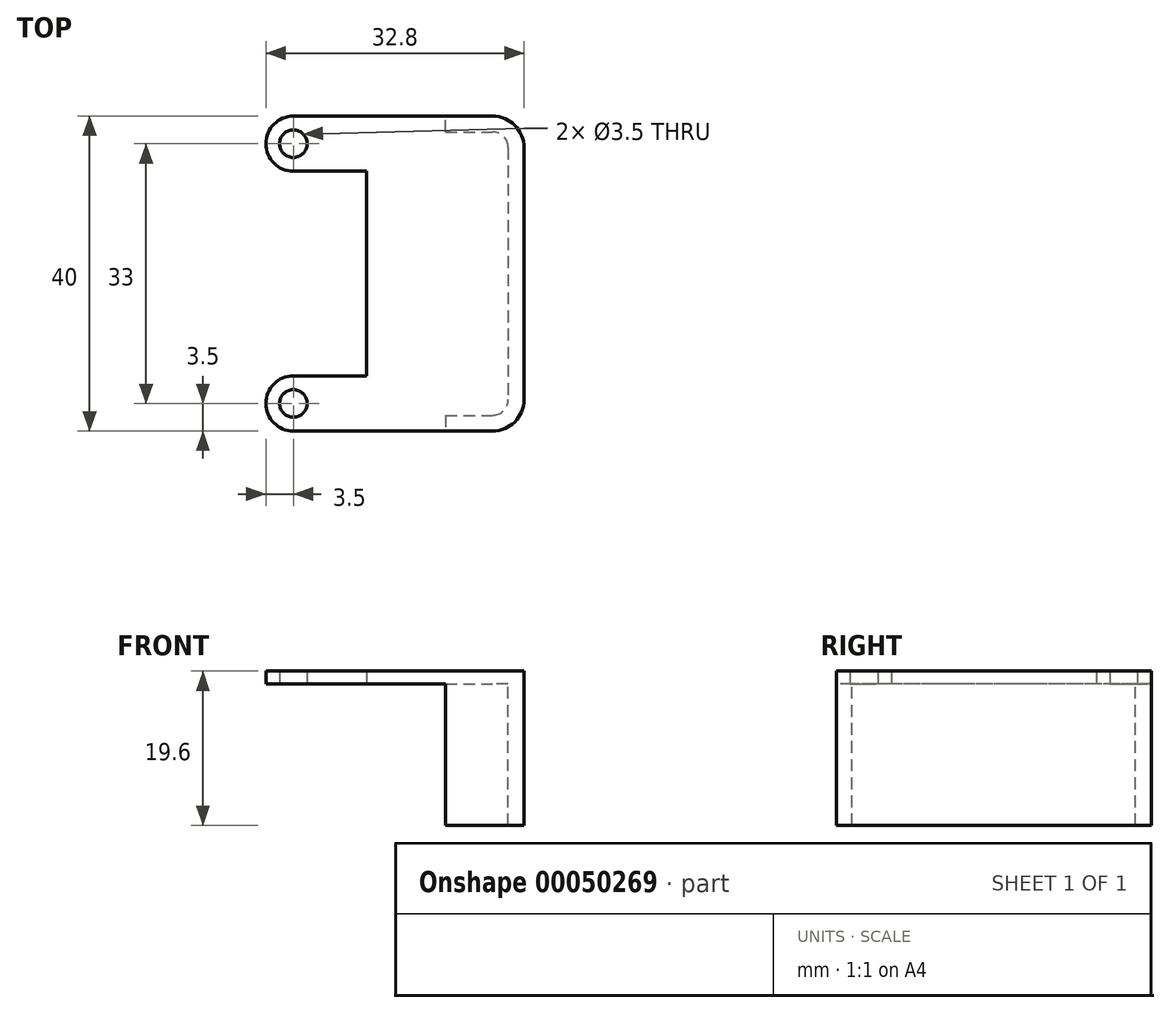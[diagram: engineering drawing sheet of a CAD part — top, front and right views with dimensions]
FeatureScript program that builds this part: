
annotation { "Feature Type Name" : "Feature", "Feature Type Description" : "" }
export const myFeature = defineFeature(function(context is Context, id is Id, definition is map)
    precondition{}
    {
        {
            var Q0;
            Q0=qCreatedBy(makeId("Top.planeOp"),FACE);
            var sketch = newSketch(context, id + "F0", { "sketchPlane" : qUnion([Q0])});
            skLineSegment(sketch, "E0.bottom", {"start": v(0, 20) * mm, "end": v(20, 20) * mm});
            skLineSegment(sketch, "E0.top", {"start": v(0, -20) * mm, "end": v(20, -20) * mm});
            skLineSegment(sketch, "E0.left", {"start": v(0, 20) * mm, "end": v(0, -20) * mm});
            skLineSegment(sketch, "E0.right", {"start": v(20, 20) * mm, "end": v(20, -20) * mm});
            skLineSegment(sketch, "E1.bottom", {"start": v(0, 20) * mm, "end": v(-9.3, 20) * mm});
            skLineSegment(sketch, "E1.top", {"start": v(0, 13) * mm, "end": v(-9.3, 13) * mm});
            skLineSegment(sketch, "E1.left", {"start": v(0, 20) * mm, "end": v(0, 13) * mm});
            skLineSegment(sketch, "E1.right", {"start": v(-9.3, 20) * mm, "end": v(-9.3, 13) * mm});
            skLineSegment(sketch, "E2.bottom", {"start": v(0, -20) * mm, "end": v(-9.3, -20) * mm});
            skLineSegment(sketch, "E2.top", {"start": v(0, -13) * mm, "end": v(-9.3, -13) * mm});
            skLineSegment(sketch, "E2.left", {"start": v(0, -20) * mm, "end": v(0, -13) * mm});
            skLineSegment(sketch, "E2.right", {"start": v(-9.3, -20) * mm, "end": v(-9.3, -13) * mm});
            skCircle(sketch, "E3", {"center": v(-9.3, -16.5) * mm, "radius": 3.5 * mm});
            skCircle(sketch, "E4", {"center": v(-9.3, 16.5) * mm, "radius": 3.5 * mm});
            skCircle(sketch, "E5", {"center": v(-9.3, 16.5) * mm, "radius": 1.75 * mm});
            skCircle(sketch, "E6", {"center": v(-9.3, -16.5) * mm, "radius": 1.75 * mm});
            skPoint(sketch, "E7", {"position": v(0, 0) * mm});
            skLineSegment(sketch, "E8.0", {"start": v(2, 18) * mm, "end": v(18, 18) * mm});
            skLineSegment(sketch, "E8.1", {"start": v(2, 18) * mm, "end": v(2, -18) * mm});
            skLineSegment(sketch, "E8.2", {"start": v(2, -18) * mm, "end": v(18, -18) * mm});
            skLineSegment(sketch, "E8.3", {"start": v(18, 18) * mm, "end": v(18, -18) * mm});
            skLineSegment(sketch, "E9", {"start": v(2, -18) * mm, "end": v(0, -20) * mm});
            skLineSegment(sketch, "E10", {"start": v(2, 18) * mm, "end": v(0, 20) * mm});
            skLineSegment(sketch, "E11", {"start": v(10, 18) * mm, "end": v(10, 20) * mm});
            skLineSegment(sketch, "E12", {"start": v(10, -18) * mm, "end": v(10, -20) * mm});
            skSolve(sketch);
        }
        {
            var Q0;
            {var subQ1=sQuery(id+"F0.wireOp",EDGE,"E1.right");var subQ3=sQuery(id+"F0.wireOp",EDGE,"E5");var subQ4=makeQuery(id+"F0.imprint","INTERSECT",VERTEX,{"disambiguationData":[OD(0.0)],"derivedFrom":[subQ1,subQ3]});Q0=makeQuery(id+"F0.imprint","IMPRINT",FACE,{"disambiguationData":[TD([[makeQuery(id+"F0.imprint","IMPRINT",EDGE,{"disambiguationData":[TD([[subQ4,-1.0]])],"derivedFrom":subQ3}),-1.0]])]});}
            var Q1;
            {var subQ1=sQuery(id+"F0.wireOp",EDGE,"E1.right");var subQ3=sQuery(id+"F0.wireOp",EDGE,"E5");var subQ4=makeQuery(id+"F0.imprint","INTERSECT",VERTEX,{"disambiguationData":[OD(0.0)],"derivedFrom":[subQ1,subQ3]});Q1=makeQuery(id+"F0.imprint","IMPRINT",FACE,{"disambiguationData":[TD([[makeQuery(id+"F0.imprint","IMPRINT",EDGE,{"disambiguationData":[TD([[subQ4,1.0]])],"derivedFrom":subQ3}),-1.0]])]});}
            var Q2;
            {var subQ0=sQuery(id+"F0.wireOp",EDGE,"E1.bottom");Q2=makeQuery(id+"F0.imprint","IMPRINT",FACE,{"disambiguationData":[TD([[makeQuery(id+"F0.imprint","IMPRINT",EDGE,{"derivedFrom":subQ0}),1.0]])]});}
            var Q3;
            {var subQ1=sQuery(id+"F0.wireOp",EDGE,"E2.right");var subQ3=sQuery(id+"F0.wireOp",EDGE,"E6");var subQ4=makeQuery(id+"F0.imprint","INTERSECT",VERTEX,{"disambiguationData":[OD(0.0)],"derivedFrom":[subQ1,subQ3]});Q3=makeQuery(id+"F0.imprint","IMPRINT",FACE,{"disambiguationData":[TD([[makeQuery(id+"F0.imprint","IMPRINT",EDGE,{"disambiguationData":[TD([[subQ4,1.0]])],"derivedFrom":subQ3}),-1.0]])]});}
            var Q4;
            {var subQ1=sQuery(id+"F0.wireOp",EDGE,"E2.right");var subQ3=sQuery(id+"F0.wireOp",EDGE,"E6");var subQ4=makeQuery(id+"F0.imprint","INTERSECT",VERTEX,{"disambiguationData":[OD(0.0)],"derivedFrom":[subQ1,subQ3]});Q4=makeQuery(id+"F0.imprint","IMPRINT",FACE,{"disambiguationData":[TD([[makeQuery(id+"F0.imprint","IMPRINT",EDGE,{"disambiguationData":[TD([[subQ4,-1.0]])],"derivedFrom":subQ3}),-1.0]])]});}
            var Q5;
            {var subQ0=sQuery(id+"F0.wireOp",EDGE,"E2.bottom");Q5=makeQuery(id+"F0.imprint","IMPRINT",FACE,{"disambiguationData":[TD([[makeQuery(id+"F0.imprint","IMPRINT",EDGE,{"derivedFrom":subQ0}),-1.0]])]});}
            var Q6;
            Q6=makeQuery(id+"F0.imprint","IMPRINT",FACE,{"disambiguationData":[TD([[makeQuery(id+"F0.imprint","IMPRINT",EDGE,{"derivedFrom":sQuery(id+"F0.wireOp",EDGE,"E0.left")}),1.0]])]});
            var Q7;
            {var subQ0=sQuery(id+"F0.wireOp",EDGE,"72b2980c-2a17-4527-adef-8bc1a54d9b44");Q7=makeQuery(id+"F0.imprint","IMPRINT",FACE,{"disambiguationData":[TD([[makeQuery(id+"F0.imprint","IMPRINT",EDGE,{"derivedFrom":subQ0}),-1.0]])]});}
            var Q8;
            {var subQ0=sQuery(id+"F0.wireOp",EDGE,"E0.right");Q8=makeQuery(id+"F0.imprint","IMPRINT",FACE,{"disambiguationData":[TD([[makeQuery(id+"F0.imprint","IMPRINT",EDGE,{"derivedFrom":subQ0}),-1.0]])]});}
            var Q9;
            Q9=makeQuery(id+"F0.imprint","IMPRINT",FACE,{"disambiguationData":[TD([[makeQuery(id+"F0.imprint","IMPRINT",EDGE,{"derivedFrom":sQuery(id+"F0.wireOp",EDGE,"E8.0")}),-1.0]])]});
            var Q10;
            Q10=makeQuery(id+"F0.imprint","IMPRINT",FACE,{"disambiguationData":[TD([[makeQuery(id+"F0.imprint","IMPRINT",EDGE,{"derivedFrom":sQuery(id+"F0.wireOp",EDGE,"E8.0")}),1.0]])]});
            var Q11;
            Q11=makeQuery(id+"F0.imprint","IMPRINT",FACE,{"disambiguationData":[TD([[makeQuery(id+"F0.imprint","IMPRINT",EDGE,{"derivedFrom":sQuery(id+"F0.wireOp",EDGE,"E8.2")}),-1.0]])]});
            extrude(context, id + "F1", {"entities" : qUnion([Q0, Q1, Q2, Q3, Q4, Q5, Q6, Q7, Q8, Q9, Q10, Q11]), "depth" : 1.6 * mm});
        }
        {
            var Q0;
            {var subQ0=sQuery(id+"F0.wireOp",EDGE,"E0.right");Q0=makeQuery(id+"F0.imprint","IMPRINT",FACE,{"disambiguationData":[TD([[makeQuery(id+"F0.imprint","IMPRINT",EDGE,{"derivedFrom":subQ0}),-1.0]])]});}
            extrude(context, id + "F2", {"entities" : qUnion([Q0]), "operationType" : NewBodyOperationType.ADD, "oppositeDirection" : true, "depth" : 18 * mm});
        }
        {
            var Q0;
            {var subQ0=sQuery(id+"F0.wireOp",EDGE,"E0.right");var subQ1=sQuery(id+"F0.wireOp",EDGE,"E0.top");Q0=makeQuery(id+"F2.boolean.opBoolean","MERGE",EDGE,{"derivedFrom":[makeQuery(id+"F1.opExtrude","SWEPT_EDGE",EDGE,{"disambiguationData":[OSD([subQ1,subQ0])]}),makeQuery(id+"F2.opExtrude","SWEPT_EDGE",EDGE,{"disambiguationData":[OSD([subQ1,subQ0])]})]});}
            var Q1;
            {var subQ0=sQuery(id+"F0.wireOp",EDGE,"E0.right");var subQ1=sQuery(id+"F0.wireOp",EDGE,"E0.bottom");Q1=makeQuery(id+"F2.boolean.opBoolean","MERGE",EDGE,{"derivedFrom":[makeQuery(id+"F1.opExtrude","SWEPT_EDGE",EDGE,{"disambiguationData":[OSD([subQ1,subQ0])]}),makeQuery(id+"F2.opExtrude","SWEPT_EDGE",EDGE,{"disambiguationData":[OSD([subQ1,subQ0])]})]});}
            fillet(context, id + "F3", {"entities" : qUnion([Q0, Q1]), "radius" : 4 * mm, "tangentPropagation" : true, "allowEdgeOverflow" : false});
        }
        {
            var Q0;
            Q0=makeQuery(id+"F2.opExtrude","SWEPT_EDGE",EDGE,{"disambiguationData":[OSD([sQuery(id+"F0.wireOp",EDGE,"E8.2"),sQuery(id+"F0.wireOp",EDGE,"E8.3")])]});
            var Q1;
            Q1=makeQuery(id+"F2.opExtrude","SWEPT_EDGE",EDGE,{"disambiguationData":[OSD([sQuery(id+"F0.wireOp",EDGE,"E8.0"),sQuery(id+"F0.wireOp",EDGE,"E8.3")])]});
            fillet(context, id + "F4", {"entities" : qUnion([Q0, Q1]), "radius" : 2 * mm, "tangentPropagation" : true, "allowEdgeOverflow" : false});
        }
    });
